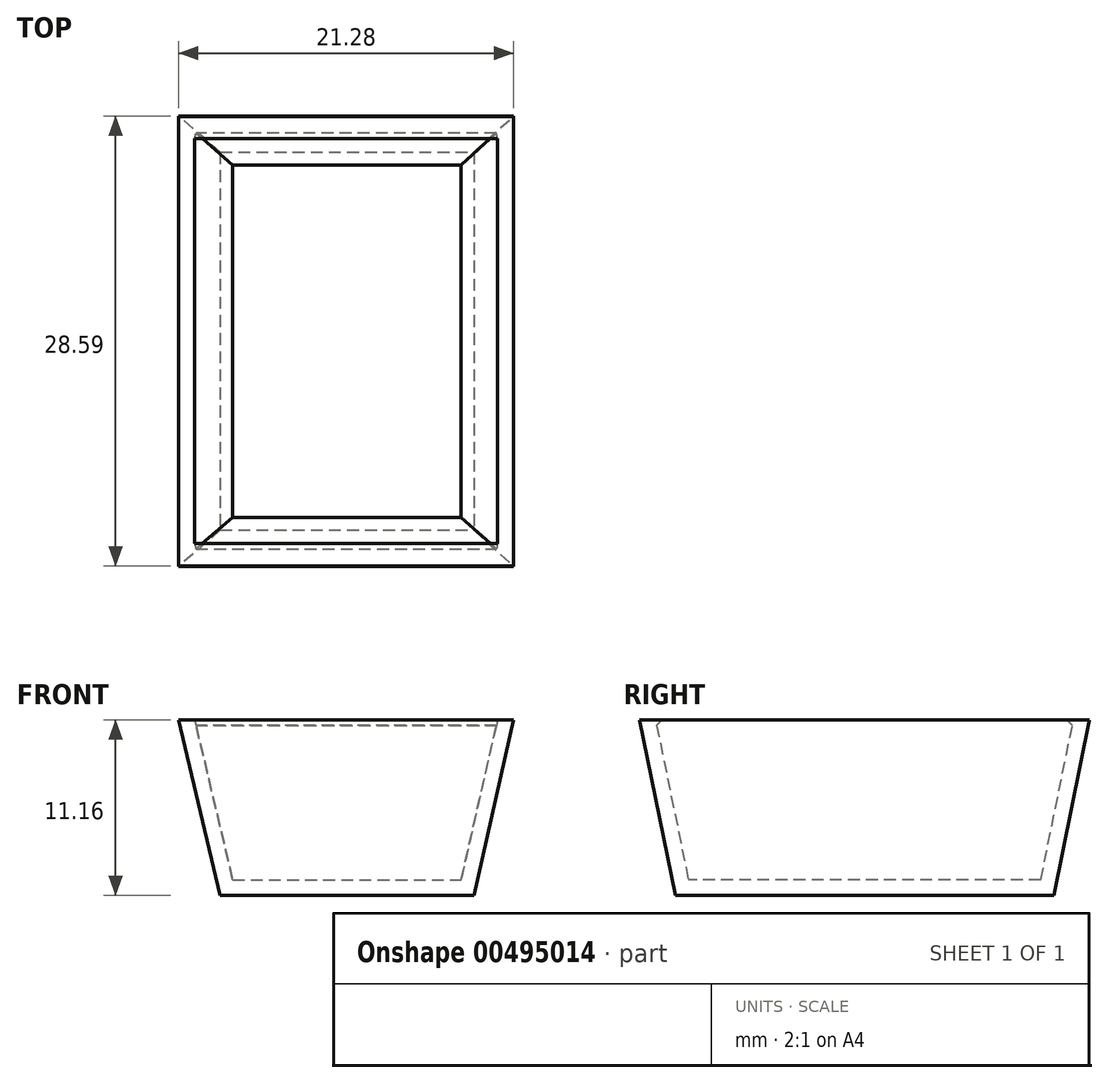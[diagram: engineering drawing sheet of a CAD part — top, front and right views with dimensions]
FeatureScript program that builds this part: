
annotation { "Feature Type Name" : "Feature", "Feature Type Description" : "" }
export const myFeature = defineFeature(function(context is Context, id is Id, definition is map)
    precondition{}
    {
        {
            var Q0;
            Q0=qCreatedBy(makeId("Top.planeOp"),FACE);
            var sketch = newSketch(context, id + "F0", { "sketchPlane" : qUnion([Q0])});
            skLineSegment(sketch, "E0.bottom", {"start": v(-7.96, 12.01) * mm, "end": v(8.14, 12.01) * mm});
            skLineSegment(sketch, "E0.top", {"start": v(-7.96, -12) * mm, "end": v(8.14, -12) * mm});
            skLineSegment(sketch, "E0.left", {"start": v(-7.96, 12.01) * mm, "end": v(-7.96, -12) * mm});
            skLineSegment(sketch, "E0.right", {"start": v(8.14, 12.01) * mm, "end": v(8.14, -12) * mm});
            skSolve(sketch);
        }
        {
            var Q0;
            Q0=makeQuery(id+"F0.imprint","IMPRINT",FACE,{"disambiguationData":[TD([[makeQuery(id+"F0.imprint","IMPRINT",EDGE,{"derivedFrom":sQuery(id+"F0.wireOp",EDGE,"E0.bottom")}),-1.0]])]});
            cPlane(context, id + "F1", {"entities" : qUnion([Q0]), "cplaneType" : CPlaneType.OFFSET, "offset" : 17 * mm, "width" : 152.4 * mm, "height" : 152.4 * mm});
        }
        {
            var Q0;
            Q0=qCreatedBy(id+"F1.planeOp",FACE);
            var sketch = newSketch(context, id + "F2", { "sketchPlane" : qUnion([Q0])});
            skLineSegment(sketch, "E1.bottom", {"start": v(-12, 15.5) * mm, "end": v(12, 15.5) * mm});
            skLineSegment(sketch, "E1.top", {"start": v(-12, -15.5) * mm, "end": v(12, -15.5) * mm});
            skLineSegment(sketch, "E1.left", {"start": v(-12, 15.5) * mm, "end": v(-12, -15.5) * mm});
            skLineSegment(sketch, "E1.right", {"start": v(12, 15.5) * mm, "end": v(12, -15.5) * mm});
            skPoint(sketch, "E2.orphan", {"position": v(0, 15.5) * mm});
            skPoint(sketch, "E3.orphan", {"position": v(12, 0) * mm});
            skPoint(sketch, "E4.start.orphan", {"position": v(-12, 0) * mm});
            skPoint(sketch, "E5.end.orphan", {"position": v(0, -15.5) * mm});
            skSolve(sketch);
        }
        {
            var Q0;
            Q0=makeQuery(id+"F0.imprint","IMPRINT",FACE,{"disambiguationData":[TD([[makeQuery(id+"F0.imprint","IMPRINT",EDGE,{"derivedFrom":sQuery(id+"F0.wireOp",EDGE,"E0.bottom")}),-1.0]])]});
            var Q1;
            Q1=makeQuery(id+"F2.imprint","IMPRINT",FACE,{"disambiguationData":[TD([[makeQuery(id+"F2.imprint","IMPRINT",EDGE,{"derivedFrom":sQuery(id+"F2.wireOp",EDGE,"E1.bottom")}),-1.0]])]});
            loft(context, id + "F3", {"sheetProfilesArray" : [{ "sheetProfileEntities" : qUnion([Q0]) }, { "sheetProfileEntities" : qUnion([Q1]) }]});
        }
        {
            var Q0;
            Q0=makeQuery(id+"F3.opLoft","CAP_FACE",FACE,{"disambiguationData":[OSD([makeQuery(id+"F2.imprint","IMPRINT",FACE,{"disambiguationData":[TD([[makeQuery(id+"F2.imprint","IMPRINT",EDGE,{"derivedFrom":sQuery(id+"F2.wireOp",EDGE,"E1.bottom")}),-1.0]])]})])],"isStart":true});
            var Q1;
            Q1=makeQuery(id+"F3.opLoft","MID_CAP_EDGE",EDGE,{"disambiguationData":[OSD([sQuery(id+"F2.wireOp",EDGE,"E1.bottom"),sQuery(id+"F2.wireOp",EDGE,"E1.top"),sQuery(id+"F2.wireOp",EDGE,"E1.left")])],"capPos":1.0});
            cPlane(context, id + "F4", {"entities" : qUnion([Q0, Q1]), "cplaneType" : CPlaneType.LINE_ANGLE, "offset" : 25.4 * mm, "angle" : 45 * degree, "width" : 152.4 * mm, "height" : 152.4 * mm});
        }
        {
            var Q0;
            Q0=qCreatedBy(id+"F4.planeOp",FACE);
            var sketch = newSketch(context, id + "F5", { "sketchPlane" : qUnion([Q0])});
            skLineSegment(sketch, "E6.bottom", {"start": v(9.14, -17.8) * mm, "end": v(-4.89, -17.8) * mm});
            skLineSegment(sketch, "E6.top", {"start": v(9.14, 17.28) * mm, "end": v(-4.89, 17.28) * mm});
            skLineSegment(sketch, "E6.left", {"start": v(9.14, -17.8) * mm, "end": v(9.14, 17.28) * mm});
            skLineSegment(sketch, "E6.right", {"start": v(-4.89, -17.8) * mm, "end": v(-4.89, 17.28) * mm});
            skSolve(sketch);
        }
        {
            var Q0;
            Q0=makeQuery(id+"F5.imprint","IMPRINT",FACE,{"disambiguationData":[TD([[makeQuery(id+"F5.imprint","IMPRINT",EDGE,{"derivedFrom":sQuery(id+"F5.wireOp",EDGE,"E6.bottom")}),-1.0]])]});
            extrude(context, id + "F6", {"entities" : qUnion([Q0]), "operationType" : NewBodyOperationType.REMOVE, "depth" : 5 * mm});
        }
        {
            var Q0;
            Q0=makeQuery(id+"F3.opLoft","CAP_FACE",FACE,{"disambiguationData":[OSD([makeQuery(id+"F2.imprint","IMPRINT",FACE,{"disambiguationData":[TD([[makeQuery(id+"F2.imprint","IMPRINT",EDGE,{"derivedFrom":sQuery(id+"F2.wireOp",EDGE,"E1.bottom")}),-1.0]])]})])],"isStart":true});
            var Q1;
            Q1=makeQuery(id+"F3.opLoft","MID_CAP_EDGE",EDGE,{"disambiguationData":[OSD([sQuery(id+"F2.wireOp",EDGE,"E1.bottom"),sQuery(id+"F2.wireOp",EDGE,"E1.top"),sQuery(id+"F2.wireOp",EDGE,"E1.right")])],"capPos":1.0});
            cPlane(context, id + "F7", {"entities" : qUnion([Q0, Q1]), "cplaneType" : CPlaneType.LINE_ANGLE, "offset" : 25.4 * mm, "angle" : 135 * degree, "width" : 152.4 * mm, "height" : 152.4 * mm});
        }
        {
            var Q0;
            Q0=qCreatedBy(id+"F7.planeOp",FACE);
            var sketch = newSketch(context, id + "F8", { "sketchPlane" : qUnion([Q0])});
            skLineSegment(sketch, "E7.bottom", {"start": v(-18.41, 11.96) * mm, "end": v(18.3, 11.96) * mm});
            skLineSegment(sketch, "E7.top", {"start": v(-18.41, -3.72) * mm, "end": v(18.3, -3.72) * mm});
            skLineSegment(sketch, "E7.left", {"start": v(-18.41, 11.96) * mm, "end": v(-18.41, -3.72) * mm});
            skLineSegment(sketch, "E7.right", {"start": v(18.3, 11.96) * mm, "end": v(18.3, -3.72) * mm});
            skSolve(sketch);
        }
        {
            var Q0;
            Q0=makeQuery(id+"F8.imprint","IMPRINT",FACE,{"disambiguationData":[TD([[makeQuery(id+"F8.imprint","IMPRINT",EDGE,{"derivedFrom":sQuery(id+"F8.wireOp",EDGE,"E7.bottom")}),-1.0]])]});
            extrude(context, id + "F9", {"entities" : qUnion([Q0]), "operationType" : NewBodyOperationType.REMOVE, "oppositeDirection" : true, "depth" : 5 * mm});
        }
        {
            var Q0;
            Q0=makeQuery(id+"F3.opLoft","CAP_FACE",FACE,{"disambiguationData":[OSD([makeQuery(id+"F2.imprint","IMPRINT",FACE,{"disambiguationData":[TD([[makeQuery(id+"F2.imprint","IMPRINT",EDGE,{"derivedFrom":sQuery(id+"F2.wireOp",EDGE,"E1.bottom")}),-1.0]])]})])],"isStart":true});
            var Q1;
            Q1=makeQuery(id+"F3.opLoft","MID_CAP_EDGE",EDGE,{"disambiguationData":[OSD([sQuery(id+"F2.wireOp",EDGE,"E1.bottom"),sQuery(id+"F2.wireOp",EDGE,"E1.left"),sQuery(id+"F2.wireOp",EDGE,"E1.right")])],"capPos":1.0});
            cPlane(context, id + "F10", {"entities" : qUnion([Q0, Q1]), "cplaneType" : CPlaneType.LINE_ANGLE, "offset" : 25.4 * mm, "angle" : 135 * degree, "width" : 152.4 * mm, "height" : 152.4 * mm});
        }
        {
            var Q0;
            Q0=qCreatedBy(id+"F10.planeOp",FACE);
            var sketch = newSketch(context, id + "F11", { "sketchPlane" : qUnion([Q0])});
            skLineSegment(sketch, "E8.bottom", {"start": v(15, -5.65) * mm, "end": v(-14.31, -5.65) * mm});
            skLineSegment(sketch, "E8.top", {"start": v(15, 13.2) * mm, "end": v(-14.31, 13.2) * mm});
            skLineSegment(sketch, "E8.left", {"start": v(15, -5.65) * mm, "end": v(15, 13.2) * mm});
            skLineSegment(sketch, "E8.right", {"start": v(-14.31, -5.65) * mm, "end": v(-14.31, 13.2) * mm});
            skSolve(sketch);
        }
        {
            var Q0;
            Q0=makeQuery(id+"F11.imprint","IMPRINT",FACE,{"disambiguationData":[TD([[makeQuery(id+"F11.imprint","IMPRINT",EDGE,{"derivedFrom":sQuery(id+"F11.wireOp",EDGE,"E8.bottom")}),-1.0]])]});
            extrude(context, id + "F12", {"entities" : qUnion([Q0]), "operationType" : NewBodyOperationType.REMOVE, "oppositeDirection" : true, "depth" : 5 * mm});
        }
        {
            var Q0;
            Q0=makeQuery(id+"F3.opLoft","CAP_FACE",FACE,{"disambiguationData":[OSD([makeQuery(id+"F2.imprint","IMPRINT",FACE,{"disambiguationData":[TD([[makeQuery(id+"F2.imprint","IMPRINT",EDGE,{"derivedFrom":sQuery(id+"F2.wireOp",EDGE,"E1.bottom")}),-1.0]])]})])],"isStart":true});
            var Q1;
            Q1=makeQuery(id+"F3.opLoft","MID_CAP_EDGE",EDGE,{"disambiguationData":[OSD([sQuery(id+"F2.wireOp",EDGE,"E1.top"),sQuery(id+"F2.wireOp",EDGE,"E1.left"),sQuery(id+"F2.wireOp",EDGE,"E1.right")])],"capPos":1.0});
            cPlane(context, id + "F13", {"entities" : qUnion([Q0, Q1]), "cplaneType" : CPlaneType.LINE_ANGLE, "offset" : 25.4 * mm, "angle" : 45 * degree, "width" : 152.4 * mm, "height" : 152.4 * mm});
        }
        {
            var Q0;
            Q0=qCreatedBy(id+"F13.planeOp",FACE);
            var sketch = newSketch(context, id + "F14", { "sketchPlane" : qUnion([Q0])});
            skLineSegment(sketch, "E9.bottom", {"start": v(-14.88, -7.25) * mm, "end": v(16.64, -7.25) * mm});
            skLineSegment(sketch, "E9.top", {"start": v(-14.88, 6.04) * mm, "end": v(16.64, 6.04) * mm});
            skLineSegment(sketch, "E9.left", {"start": v(-14.88, -7.25) * mm, "end": v(-14.88, 6.04) * mm});
            skLineSegment(sketch, "E9.right", {"start": v(16.64, -7.25) * mm, "end": v(16.64, 6.04) * mm});
            skSolve(sketch);
        }
        {
            var Q0;
            Q0=makeQuery(id+"F14.imprint","IMPRINT",FACE,{"disambiguationData":[TD([[makeQuery(id+"F14.imprint","IMPRINT",EDGE,{"derivedFrom":sQuery(id+"F14.wireOp",EDGE,"E9.bottom")}),1.0]])]});
            extrude(context, id + "F15", {"entities" : qUnion([Q0]), "operationType" : NewBodyOperationType.REMOVE, "depth" : 5 * mm});
        }
        {
            var Q0;
            Q0=qCreatedBy(makeId("Front.planeOp"),FACE);
            var sketch = newSketch(context, id + "F16", { "sketchPlane" : qUnion([Q0])});
            skLineSegment(sketch, "E10.bottom", {"start": v(11.07, 11.16) * mm, "end": v(-13.83, 11.16) * mm});
            skLineSegment(sketch, "E10.top", {"start": v(11.07, 19) * mm, "end": v(-13.83, 19) * mm});
            skLineSegment(sketch, "E10.left", {"start": v(11.07, 11.16) * mm, "end": v(11.07, 19) * mm});
            skLineSegment(sketch, "E10.right", {"start": v(-13.83, 11.16) * mm, "end": v(-13.83, 19) * mm});
            skSolve(sketch);
        }
        {
            var Q0;
            Q0=makeQuery(id+"F16.imprint","IMPRINT",FACE,{"disambiguationData":[TD([[makeQuery(id+"F16.imprint","IMPRINT",EDGE,{"derivedFrom":sQuery(id+"F16.wireOp",EDGE,"E10.bottom")}),-1.0]])]});
            extrude(context, id + "F17", {"entities" : qUnion([Q0]), "operationType" : NewBodyOperationType.REMOVE, "endBound" : BoundingType.SYMMETRIC, "oppositeDirection" : true, "depth" : 50.8 * mm});
        }
        {
            var Q0;
            Q0=makeQuery(id+"F17.boolean.opBoolean","COPY",FACE,{"derivedFrom":makeQuery(id+"F17.opExtrude","SWEPT_FACE",FACE,{"disambiguationData":[OSD([sQuery(id+"F16.wireOp",EDGE,"E10.bottom")])]})});
            shell(context, id + "F18", {"entities" : qUnion([Q0]), "thickness" : 1 * mm});
        }
    });
